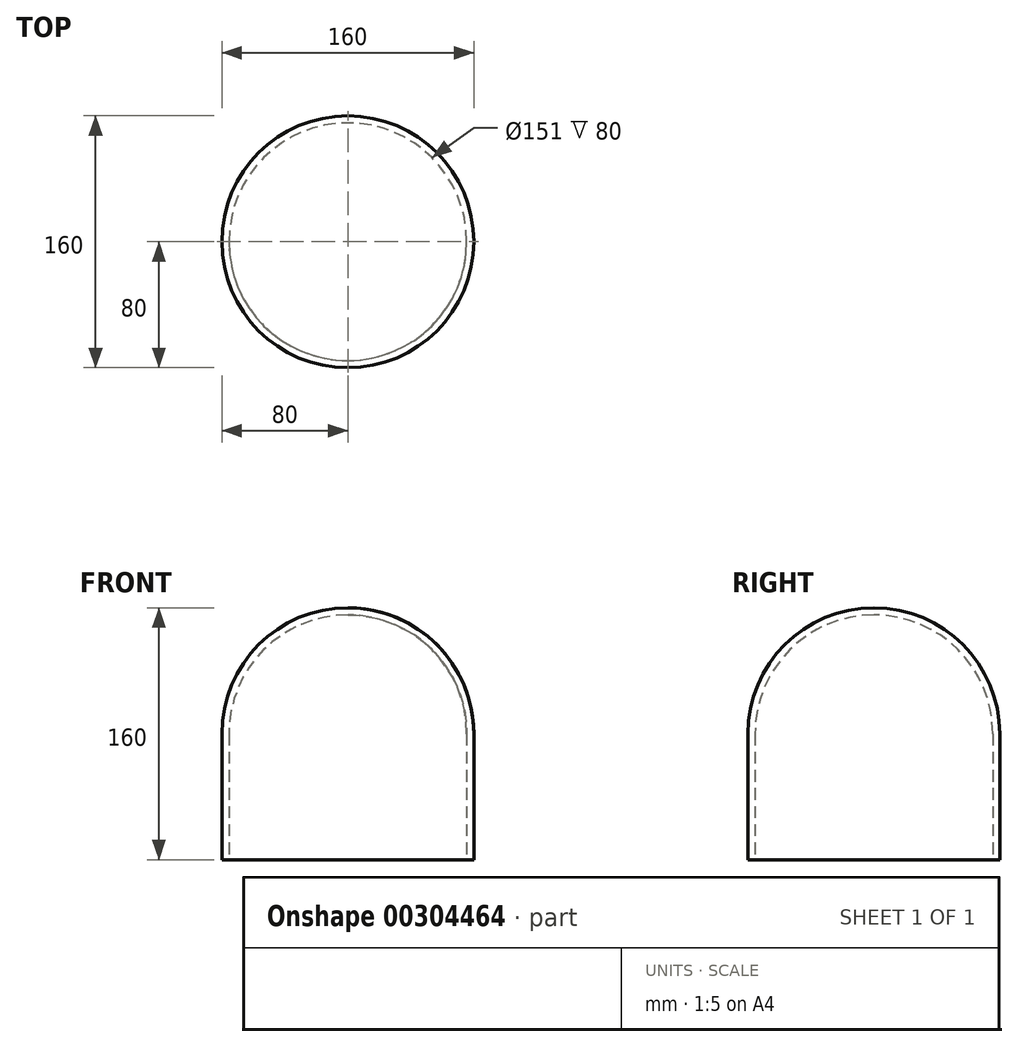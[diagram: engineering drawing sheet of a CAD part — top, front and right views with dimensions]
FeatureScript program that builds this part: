
annotation { "Feature Type Name" : "Feature", "Feature Type Description" : "" }
export const myFeature = defineFeature(function(context is Context, id is Id, definition is map)
    precondition{}
    {
        {
            var Q0;
            Q0=qCreatedBy(makeId("Front.planeOp"),FACE);
            var sketch = newSketch(context, id + "F0", { "sketchPlane" : qUnion([Q0])});
            skLineSegment(sketch, "E0", {"start": v(0, 0) * mm, "end": v(0, 160) * mm, "construction": true});
            skPoint(sketch, "E1", {"position": v(0, 80) * mm});
            skLineSegment(sketch, "E2", {"start": v(0, 80) * mm, "end": v(-113.56, 80) * mm, "construction": true});
            skArc(sketch, "E3", {"start": v(-80, 80) * mm, "mid": v(-56.57, 136.57) * mm, "end": v(0, 160) * mm});
            skLineSegment(sketch, "E4", {"start": v(-80, 80) * mm, "end": v(-80, 0) * mm});
            skLineSegment(sketch, "E5", {"start": v(-80, 0) * mm, "end": v(0, 0) * mm});
            skLineSegment(sketch, "E6", {"start": v(0, 0) * mm, "end": v(0, 160) * mm});
            skSolve(sketch);
        }
        {
            var Q0;
            Q0 = qSketchRegion(id + "F0", true);
            var Q1;
            Q1=sQuery(id+"F0.wireOp",EDGE,"E6");
            revolve(context, id + "F1", {"entities" : qUnion([Q0]), "axis" : qUnion([Q1]), "revolveType" : RevolveType.ONE_DIRECTION, "angle" : 360 * degree});
        }
        {
            var Q0;
            Q0=makeQuery(id+"F1.opRevolve","SWEPT_FACE",FACE,{"disambiguationData":[OSD([sQuery(id+"F0.wireOp",EDGE,"E5")])]});
            shell(context, id + "F2", {"entities" : qUnion([Q0]), "thickness" : 4.5 * mm});
        }
    });
